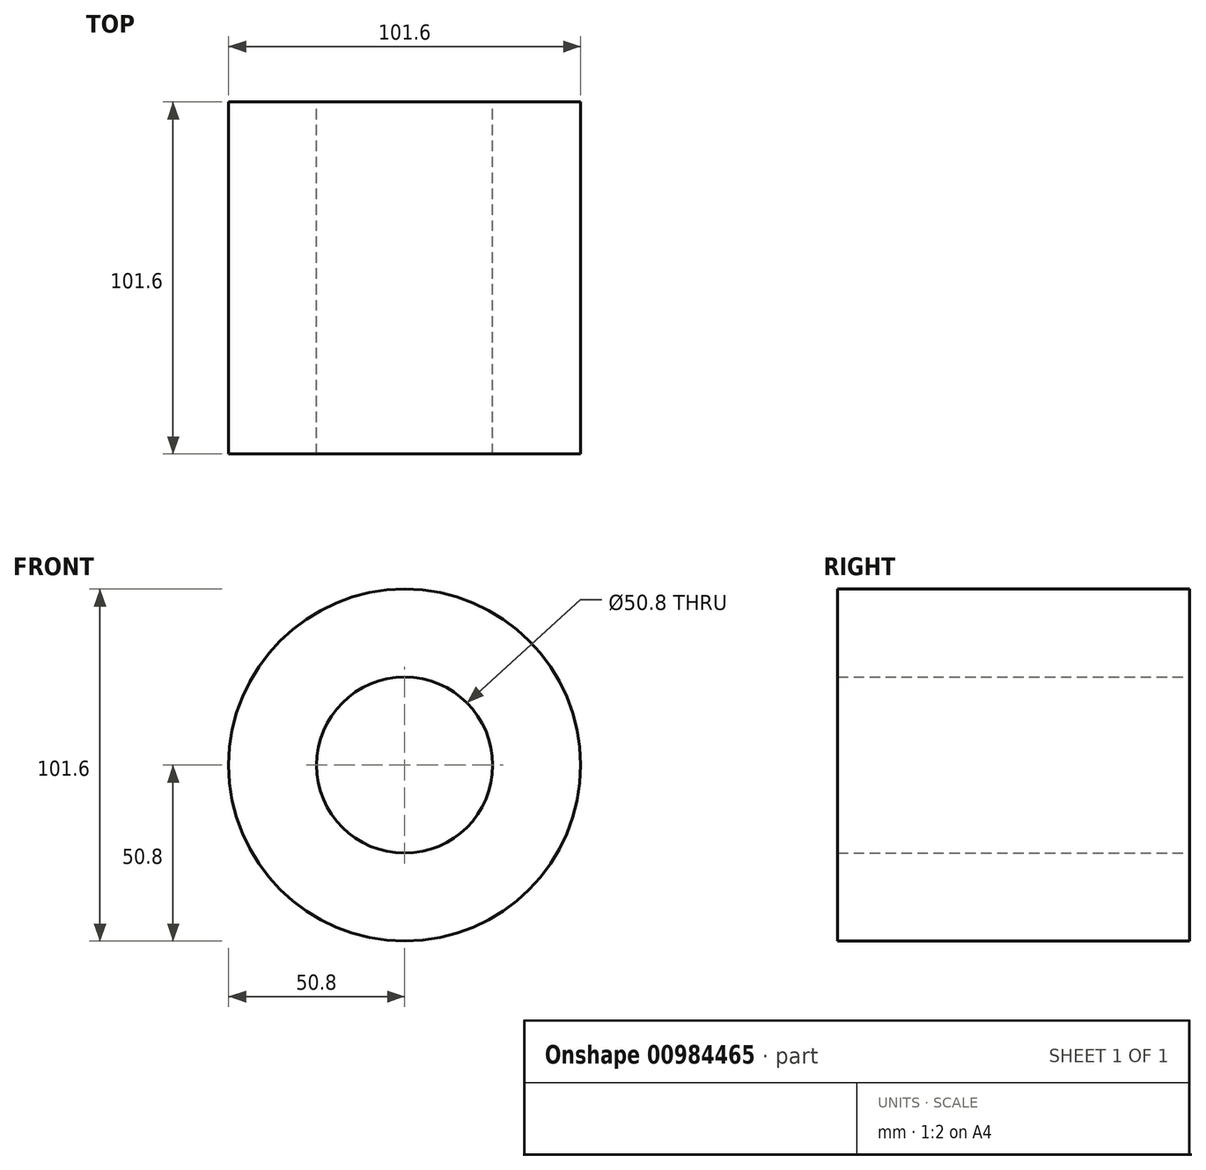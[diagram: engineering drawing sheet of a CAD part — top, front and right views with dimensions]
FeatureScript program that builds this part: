
annotation { "Feature Type Name" : "Feature", "Feature Type Description" : "" }
export const myFeature = defineFeature(function(context is Context, id is Id, definition is map)
    precondition{}
    {
        {
            var Q0;
            Q0=qCreatedBy(makeId("Front.planeOp"),FACE);
            var sketch = newSketch(context, id + "F0", { "sketchPlane" : qUnion([Q0])});
            skCircle(sketch, "E0", {"center": v(0, 0) * mm, "radius": 25.4 * mm});
            skCircle(sketch, "E1", {"center": v(0, 0) * mm, "radius": 50.8 * mm});
            skSolve(sketch);
        }
        {
            var Q0;
            Q0 = qSketchRegion(id + "F0", true);
            extrude(context, id + "F1", {"entities" : qUnion([Q0]), "depth" : 101.6 * mm, "offsetDistance" : 25.4 * mm});
        }
    });
